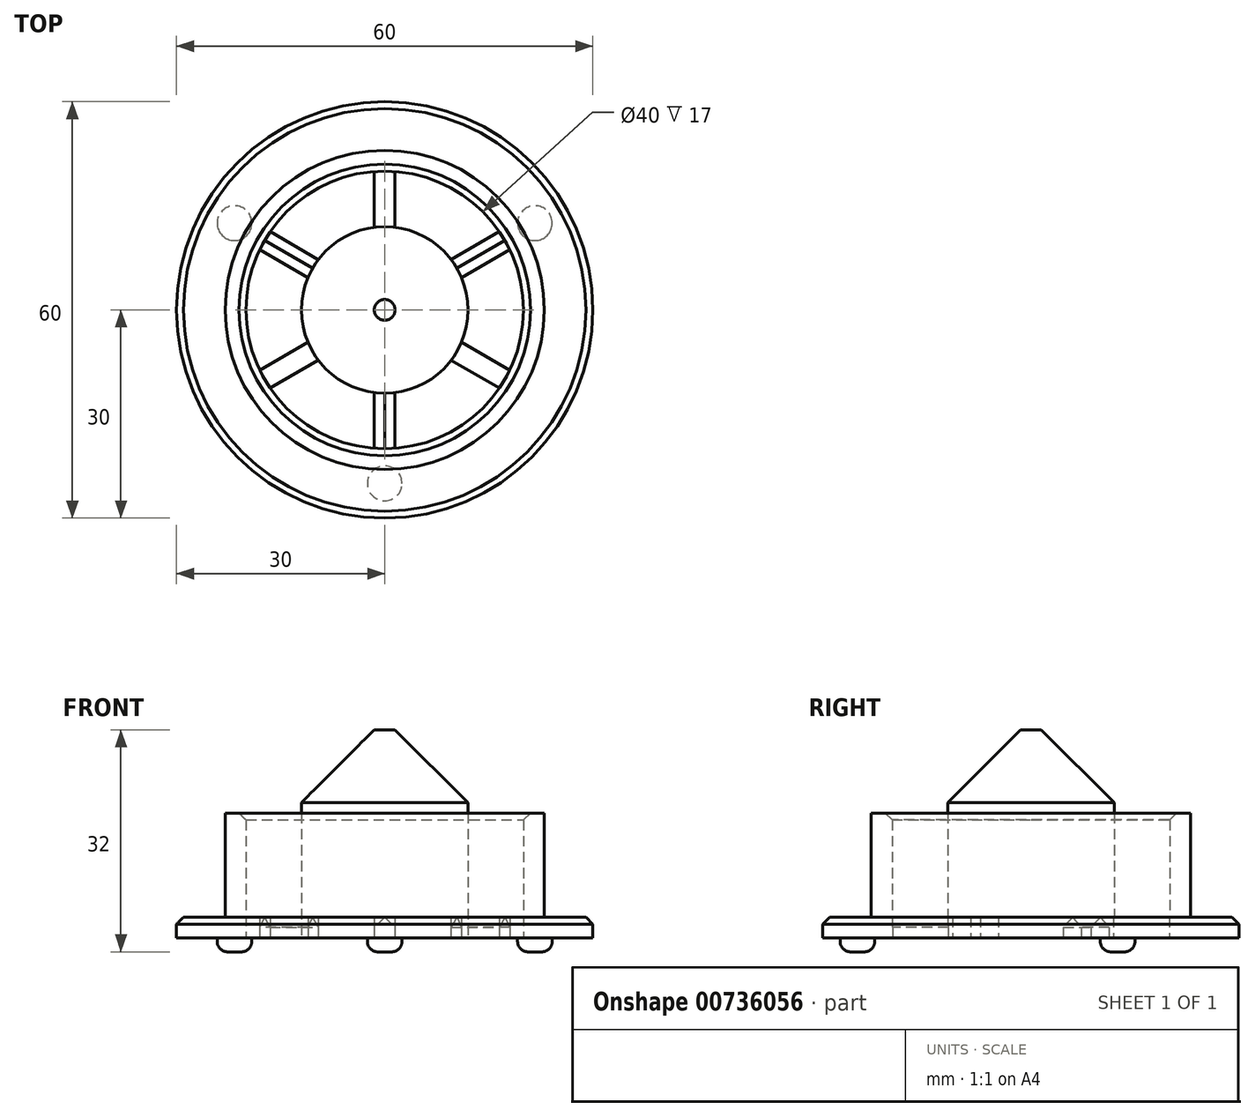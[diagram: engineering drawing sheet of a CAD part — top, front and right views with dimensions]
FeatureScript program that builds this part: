
annotation { "Feature Type Name" : "Feature", "Feature Type Description" : "" }
export const myFeature = defineFeature(function(context is Context, id is Id, definition is map)
    precondition{}
    {
        {
            var Q0;
            Q0=qCreatedBy(makeId("Front.planeOp"),FACE);
            var sketch = newSketch(context, id + "F0", { "sketchPlane" : qUnion([Q0])});
            skLineSegment(sketch, "E0", {"start": v(0, 0) * mm, "end": v(0, 73.37) * mm, "construction": true});
            skLineSegment(sketch, "E1", {"start": v(0, 0) * mm, "end": v(0, 30) * mm});
            skLineSegment(sketch, "E2", {"start": v(-12, 19.5) * mm, "end": v(-12, 3) * mm});
            skLineSegment(sketch, "E3", {"start": v(-12, 3) * mm, "end": v(-20, 3) * mm});
            skLineSegment(sketch, "E4", {"start": v(-20, 3) * mm, "end": v(-20, 18) * mm});
            skLineSegment(sketch, "E5", {"start": v(-20, 18) * mm, "end": v(-23, 18) * mm});
            skLineSegment(sketch, "E6", {"start": v(-23, 18) * mm, "end": v(-23, 3) * mm});
            skLineSegment(sketch, "E7", {"start": v(-23, 3) * mm, "end": v(-30, 3) * mm});
            skLineSegment(sketch, "E8", {"start": v(-30, 3) * mm, "end": v(-30, 0) * mm});
            skLineSegment(sketch, "E9", {"start": v(-30, 0) * mm, "end": v(0, 0) * mm});
            skLineSegment(sketch, "E10", {"start": v(0, 30) * mm, "end": v(-1.5, 30) * mm});
            skLineSegment(sketch, "E11", {"start": v(-1.5, 30) * mm, "end": v(-12, 19.5) * mm});
            skSolve(sketch);
        }
        {
            var Q0;
            Q0 = qSketchRegion(id + "F0", true);
            var Q1;
            Q1=sQuery(id+"F0.wireOp",EDGE,"E0");
            revolve(context, id + "F1", {"surfaceOperationType" : NewSurfaceOperationType.NEW, "entities" : qUnion([Q0]), "axis" : qUnion([Q1]), "revolveType" : RevolveType.FULL});
        }
        {
            var Q0;
            Q0=makeQuery(id+"F1.opRevolve","SWEPT_EDGE",EDGE,{"disambiguationData":[OSD([sQuery(id+"F0.wireOp",EDGE,"E4"),sQuery(id+"F0.wireOp",EDGE,"E5")])]});
            var Q1;
            Q1=makeQuery(id+"F1.opRevolve","SWEPT_EDGE",EDGE,{"disambiguationData":[OSD([sQuery(id+"F0.wireOp",EDGE,"E7"),sQuery(id+"F0.wireOp",EDGE,"E8")])]});
            chamfer(context, id + "F2", {"entities" : qUnion([Q0, Q1]), "width" : 1 * mm, "tangentPropagation" : true});
        }
        {
            var Q0;
            Q0=makeQuery(id+"F1.opRevolve","SWEPT_FACE",FACE,{"disambiguationData":[OSD([sQuery(id+"F0.wireOp",EDGE,"E9")])]});
            var sketch = newSketch(context, id + "F3", { "sketchPlane" : qUnion([Q0])});
            skArc(sketch, "E12", {"start": v(-1.5, 11.9) * mm, "mid": v(-6, 10.4) * mm, "end": v(-9.56, 7.25) * mm});
            skArc(sketch, "E13", {"start": v(-1.5, 19.94) * mm, "mid": v(-10, 17.32) * mm, "end": v(-16.52, 11.27) * mm});
            skLineSegment(sketch, "E14", {"start": v(0, 0) * mm, "end": v(0, 31.57) * mm, "construction": true});
            skLineSegment(sketch, "E15", {"start": v(0, 0) * mm, "end": v(28.51, -16.46) * mm, "construction": true});
            skLineSegment(sketch, "E16", {"start": v(0, 0) * mm, "end": v(-29.2, -16.86) * mm, "construction": true});
            skLineSegment(sketch, "E17", {"start": v(-1.5, 11.9) * mm, "end": v(-1.5, 19.94) * mm});
            skLineSegment(sketch, "E18.MirrorCS", {"start": v(1.5, 11.9) * mm, "end": v(1.5, 19.94) * mm});
            skLineSegment(sketch, "E19.MirrorCS", {"start": v(9.56, -7.25) * mm, "end": v(16.52, -11.27) * mm});
            skLineSegment(sketch, "E20.MirrorCS", {"start": v(11.06, -4.65) * mm, "end": v(18.02, -8.67) * mm});
            skLineSegment(sketch, "E21.MirrorCS", {"start": v(-9.56, -7.25) * mm, "end": v(-16.52, -11.27) * mm});
            skLineSegment(sketch, "E22.MirrorCS", {"start": v(-11.06, -4.65) * mm, "end": v(-18.02, -8.67) * mm});
            skArc(sketch, "E23.trimOffspring", {"start": v(-9.56, -7.25) * mm, "mid": v(-6, -10.4) * mm, "end": v(-1.5, -11.9) * mm});
            skArc(sketch, "E24.trimOffspring", {"start": v(-16.52, -11.27) * mm, "mid": v(-10, -17.32) * mm, "end": v(-1.5, -19.94) * mm});
            skArc(sketch, "E25.trimOffspring", {"start": v(11.06, -4.65) * mm, "mid": v(12, 0) * mm, "end": v(11.06, 4.65) * mm});
            skArc(sketch, "E26.trimOffspring", {"start": v(18.02, -8.67) * mm, "mid": v(20, 0) * mm, "end": v(18.02, 8.67) * mm});
            skCircle(sketch, "E27", {"center": v(0, 0) * mm, "radius": 30 * mm});
            skCircle(sketch, "E28", {"center": v(0, 25) * mm, "radius": 2.5 * mm});
            skCircle(sketch, "E29", {"center": v(21.65, -12.5) * mm, "radius": 2.5 * mm});
            skCircle(sketch, "E30", {"center": v(-21.65, -12.5) * mm, "radius": 2.5 * mm});
            skLineSegment(sketch, "E31", {"start": v(0, 0) * mm, "end": v(-29.2, 16.86) * mm, "construction": true});
            skLineSegment(sketch, "E32", {"start": v(0, 0) * mm, "end": v(0, -31.49) * mm, "construction": true});
            skPoint(sketch, "E32.endSnap0", {"position": v(0, -20) * mm});
            skLineSegment(sketch, "E33", {"start": v(0, 0) * mm, "end": v(27.87, 16.1) * mm, "construction": true});
            skLineSegment(sketch, "E34", {"start": v(-39.17, 0) * mm, "end": v(42.33, 0) * mm, "construction": true});
            skLineSegment(sketch, "E35.MirrorCS", {"start": v(-1.5, -11.9) * mm, "end": v(-1.5, -19.94) * mm});
            skLineSegment(sketch, "E36.MirrorCS", {"start": v(1.5, -11.9) * mm, "end": v(1.5, -19.94) * mm});
            skLineSegment(sketch, "E37.MirrorCS", {"start": v(9.56, 7.25) * mm, "end": v(16.52, 11.27) * mm});
            skLineSegment(sketch, "E38.MirrorCS", {"start": v(11.06, 4.65) * mm, "end": v(18.02, 8.67) * mm});
            skLineSegment(sketch, "E39.MirrorCS", {"start": v(-9.56, 7.25) * mm, "end": v(-16.52, 11.27) * mm});
            skLineSegment(sketch, "E40.MirrorCS", {"start": v(-11.06, 4.65) * mm, "end": v(-18.02, 8.67) * mm});
            skArc(sketch, "E41.trimOffspring", {"start": v(-11.06, 4.65) * mm, "mid": v(-12, 0) * mm, "end": v(-11.06, -4.65) * mm});
            skArc(sketch, "E42.trimOffspring", {"start": v(-18.02, 8.67) * mm, "mid": v(-20, 0) * mm, "end": v(-18.02, -8.67) * mm});
            skArc(sketch, "E43.trimOffspring", {"start": v(9.56, 7.25) * mm, "mid": v(6, 10.4) * mm, "end": v(1.5, 11.9) * mm});
            skArc(sketch, "E44.trimOffspring", {"start": v(16.52, 11.27) * mm, "mid": v(10, 17.32) * mm, "end": v(1.5, 19.94) * mm});
            skArc(sketch, "E45.trimOffspring", {"start": v(1.5, -11.9) * mm, "mid": v(6, -10.4) * mm, "end": v(9.56, -7.25) * mm});
            skArc(sketch, "E46.trimOffspring", {"start": v(1.5, -19.94) * mm, "mid": v(10, -17.32) * mm, "end": v(16.52, -11.27) * mm});
            skSolve(sketch);
        }
        {
            var Q0;
            Q0=makeQuery(id+"F3.imprint","IMPRINT",FACE,{"disambiguationData":[TD([[makeQuery(id+"F3.imprint","IMPRINT",EDGE,{"derivedFrom":sQuery(id+"F3.wireOp",EDGE,"E21.MirrorCS")}),1.0]])]});
            var Q1;
            Q1=makeQuery(id+"F3.imprint","IMPRINT",FACE,{"disambiguationData":[TD([[makeQuery(id+"F3.imprint","IMPRINT",EDGE,{"derivedFrom":sQuery(id+"F3.wireOp",EDGE,"E19.MirrorCS")}),-1.0]])]});
            var Q2;
            Q2=makeQuery(id+"F3.imprint","IMPRINT",FACE,{"disambiguationData":[TD([[makeQuery(id+"F3.imprint","IMPRINT",EDGE,{"derivedFrom":sQuery(id+"F3.wireOp",EDGE,"E25.trimOffspring")}),-1.0]])]});
            var Q3;
            Q3=makeQuery(id+"F3.imprint","IMPRINT",FACE,{"disambiguationData":[TD([[makeQuery(id+"F3.imprint","IMPRINT",EDGE,{"derivedFrom":sQuery(id+"F3.wireOp",EDGE,"E18.MirrorCS")}),-1.0]])]});
            var Q4;
            Q4=makeQuery(id+"F3.imprint","IMPRINT",FACE,{"disambiguationData":[TD([[makeQuery(id+"F3.imprint","IMPRINT",EDGE,{"derivedFrom":sQuery(id+"F3.wireOp",EDGE,"E12")}),-1.0]])]});
            var Q5;
            Q5=makeQuery(id+"F3.imprint","IMPRINT",FACE,{"disambiguationData":[TD([[makeQuery(id+"F3.imprint","IMPRINT",EDGE,{"derivedFrom":sQuery(id+"F3.wireOp",EDGE,"E22.MirrorCS")}),-1.0]])]});
            extrude(context, id + "F4", {"entities" : qUnion([Q0, Q1, Q2, Q3, Q4, Q5]), "operationType" : NewBodyOperationType.REMOVE, "oppositeDirection" : true, "depth" : 25 * mm, "offsetDistance" : 25 * mm});
        }
        {
            var Q0;
            Q0=makeQuery(id+"F3.imprint","IMPRINT",FACE,{"disambiguationData":[TD([[makeQuery(id+"F3.imprint","IMPRINT",EDGE,{"derivedFrom":sQuery(id+"F3.wireOp",EDGE,"E28")}),1.0]])]});
            var Q1;
            Q1=makeQuery(id+"F3.imprint","IMPRINT",FACE,{"disambiguationData":[TD([[makeQuery(id+"F3.imprint","IMPRINT",EDGE,{"derivedFrom":sQuery(id+"F3.wireOp",EDGE,"E30")}),1.0]])]});
            var Q2;
            Q2=makeQuery(id+"F3.imprint","IMPRINT",FACE,{"disambiguationData":[TD([[makeQuery(id+"F3.imprint","IMPRINT",EDGE,{"derivedFrom":sQuery(id+"F3.wireOp",EDGE,"E29")}),1.0]])]});
            extrude(context, id + "F5", {"entities" : qUnion([Q0, Q1, Q2]), "operationType" : NewBodyOperationType.ADD, "depth" : 2 * mm, "offsetDistance" : 25 * mm});
        }
        {
            var Q0;
            Q0=makeQuery(id+"F5.opExtrude","CAP_FACE",FACE,{"disambiguationData":[OSD([sQuery(id+"F3.wireOp",EDGE,"E28")])],"isStart":false});
            var Q1;
            Q1=makeQuery(id+"F5.opExtrude","CAP_FACE",FACE,{"disambiguationData":[OSD([sQuery(id+"F3.wireOp",EDGE,"E30")])],"isStart":false});
            var Q2;
            Q2=makeQuery(id+"F5.opExtrude","CAP_FACE",FACE,{"disambiguationData":[OSD([sQuery(id+"F3.wireOp",EDGE,"E29")])],"isStart":false});
            fillet(context, id + "F6", {"entities" : qUnion([Q0, Q1, Q2]), "radius" : 1.5 * mm, "tangentPropagation" : true, "allowEdgeOverflow" : false});
        }
        {
            var Q0;
            Q0=makeQuery(id+"F4.boolean.opBoolean","INTERSECT",EDGE,{"derivedFrom":[makeQuery(id+"F1.opRevolve","SWEPT_FACE",FACE,{"disambiguationData":[OSD([sQuery(id+"F0.wireOp",EDGE,"E3")])]}),makeQuery(id+"F4.opExtrude","SWEPT_FACE",FACE,{"disambiguationData":[OSD([sQuery(id+"F3.wireOp",EDGE,"E22.MirrorCS")])]})]});
            var Q1;
            Q1=makeQuery(id+"F4.boolean.opBoolean","INTERSECT",EDGE,{"derivedFrom":[makeQuery(id+"F1.opRevolve","SWEPT_FACE",FACE,{"disambiguationData":[OSD([sQuery(id+"F0.wireOp",EDGE,"E3")])]}),makeQuery(id+"F4.opExtrude","SWEPT_FACE",FACE,{"disambiguationData":[OSD([sQuery(id+"F3.wireOp",EDGE,"E21.MirrorCS")])]})]});
            var Q2;
            Q2=makeQuery(id+"F4.boolean.opBoolean","INTERSECT",EDGE,{"derivedFrom":[makeQuery(id+"F1.opRevolve","SWEPT_FACE",FACE,{"disambiguationData":[OSD([sQuery(id+"F0.wireOp",EDGE,"E3")])]}),makeQuery(id+"F4.opExtrude","SWEPT_FACE",FACE,{"disambiguationData":[OSD([sQuery(id+"F3.wireOp",EDGE,"E20.MirrorCS")])]})]});
            var Q3;
            Q3=makeQuery(id+"F4.boolean.opBoolean","INTERSECT",EDGE,{"derivedFrom":[makeQuery(id+"F1.opRevolve","SWEPT_FACE",FACE,{"disambiguationData":[OSD([sQuery(id+"F0.wireOp",EDGE,"E3")])]}),makeQuery(id+"F4.opExtrude","SWEPT_FACE",FACE,{"disambiguationData":[OSD([sQuery(id+"F3.wireOp",EDGE,"E19.MirrorCS")])]})]});
            var Q4;
            Q4=makeQuery(id+"F4.boolean.opBoolean","INTERSECT",EDGE,{"derivedFrom":[makeQuery(id+"F1.opRevolve","SWEPT_FACE",FACE,{"disambiguationData":[OSD([sQuery(id+"F0.wireOp",EDGE,"E3")])]}),makeQuery(id+"F4.opExtrude","SWEPT_FACE",FACE,{"disambiguationData":[OSD([sQuery(id+"F3.wireOp",EDGE,"E18.MirrorCS")])]})]});
            var Q5;
            Q5=makeQuery(id+"F4.boolean.opBoolean","INTERSECT",EDGE,{"derivedFrom":[makeQuery(id+"F1.opRevolve","SWEPT_FACE",FACE,{"disambiguationData":[OSD([sQuery(id+"F0.wireOp",EDGE,"E3")])]}),makeQuery(id+"F4.opExtrude","SWEPT_FACE",FACE,{"disambiguationData":[OSD([sQuery(id+"F3.wireOp",EDGE,"E17")])]})]});
            chamfer(context, id + "F7", {"entities" : qUnion([Q0, Q1, Q2, Q3, Q4, Q5]), "width" : 1.5 * mm, "tangentPropagation" : true});
        }
    });
